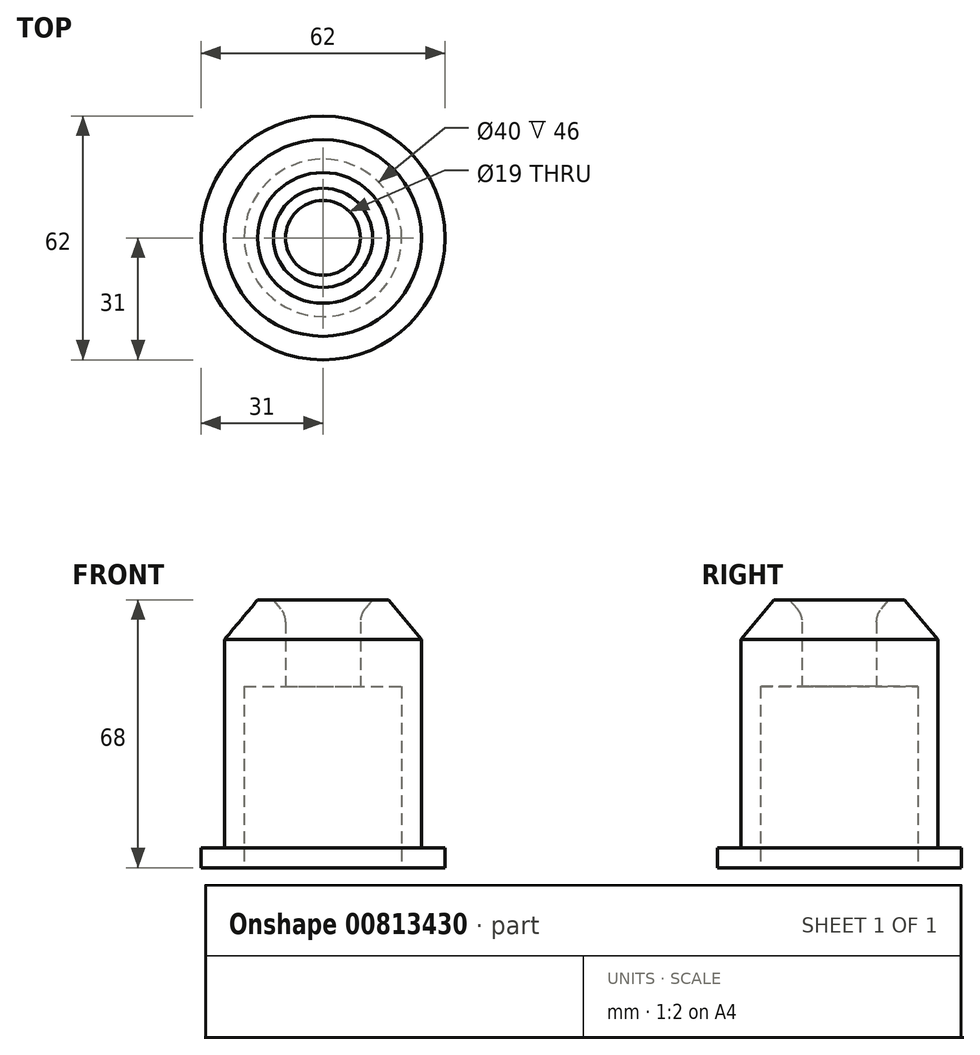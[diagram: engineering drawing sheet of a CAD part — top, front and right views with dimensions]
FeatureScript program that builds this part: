
annotation { "Feature Type Name" : "Feature", "Feature Type Description" : "" }
export const myFeature = defineFeature(function(context is Context, id is Id, definition is map)
    precondition{}
    {
        {
            var Q0;
            Q0=qCreatedBy(makeId("Front.planeOp"),FACE);
            var sketch = newSketch(context, id + "F0", { "sketchPlane" : qUnion([Q0])});
            skLineSegment(sketch, "E0", {"start": v(-20, 0) * mm, "end": v(-20, 46) * mm});
            skLineSegment(sketch, "E1", {"start": v(-20, 46) * mm, "end": v(-9.5, 46) * mm});
            skLineSegment(sketch, "E2", {"start": v(-9.5, 46) * mm, "end": v(-9.5, 64.3) * mm});
            skLineSegment(sketch, "E3", {"start": v(-12.6, 68) * mm, "end": v(-16.6, 68) * mm});
            skLineSegment(sketch, "E4", {"start": v(-16.6, 68) * mm, "end": v(-25, 58) * mm});
            skLineSegment(sketch, "E5", {"start": v(-25, 58) * mm, "end": v(-25, 5) * mm});
            skLineSegment(sketch, "E6", {"start": v(-25, 5) * mm, "end": v(-31, 5) * mm});
            skLineSegment(sketch, "E7", {"start": v(-31, 5) * mm, "end": v(-31, 0) * mm});
            skLineSegment(sketch, "E8", {"start": v(-31, 0) * mm, "end": v(-20, 0) * mm});
            skLineSegment(sketch, "E9", {"start": v(0, 0) * mm, "end": v(0, 68) * mm, "construction": true});
            skLineSegment(sketch, "E10", {"start": v(-12.6, 68) * mm, "end": v(-9.5, 64.3) * mm});
            skSolve(sketch);
        }
        {
            var Q0;
            Q0=makeQuery(id+"F0.imprint","IMPRINT",FACE,{"disambiguationData":[TD([[makeQuery(id+"F0.imprint","IMPRINT",EDGE,{"derivedFrom":sQuery(id+"F0.wireOp",EDGE,"E0")}),1.0]])]});
            var Q1;
            Q1=sQuery(id+"F0.wireOp",EDGE,"E9");
            revolve(context, id + "F1", {"surfaceOperationType" : NewSurfaceOperationType.NEW, "entities" : qUnion([Q0]), "axis" : qUnion([Q1]), "revolveType" : RevolveType.FULL});
        }
        {
            var Q0;
            Q0=makeQuery(id+"F1.opRevolve","SWEPT_EDGE",EDGE,{"disambiguationData":[OSD([sQuery(id+"F0.wireOp",EDGE,"E2"),sQuery(id+"F0.wireOp",EDGE,"E10")])]});
            fillet(context, id + "F2", {"entities" : qUnion([Q0]), "radius" : 5 * mm, "tangentPropagation" : true, "allowEdgeOverflow" : false});
        }
    });
